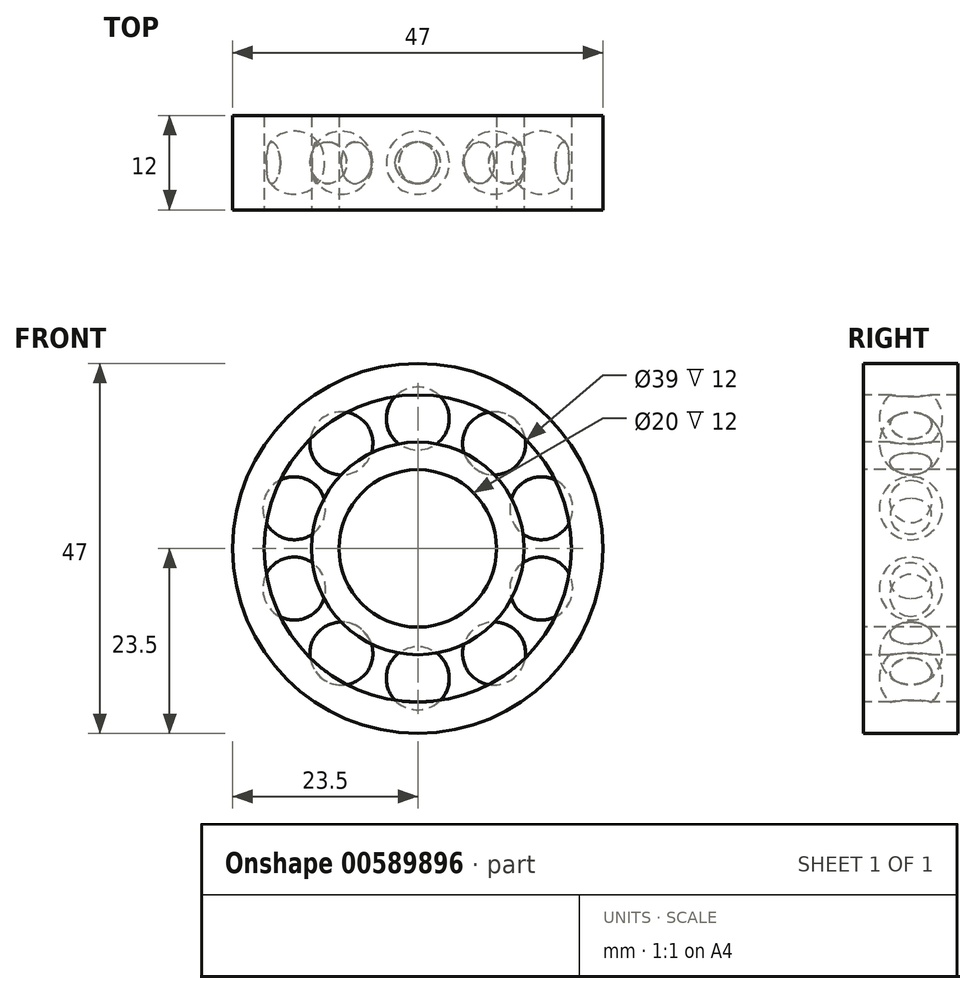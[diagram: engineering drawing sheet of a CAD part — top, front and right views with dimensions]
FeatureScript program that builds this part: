
annotation { "Feature Type Name" : "Feature", "Feature Type Description" : "" }
export const myFeature = defineFeature(function(context is Context, id is Id, definition is map)
    precondition{}
    {
        {
            var Q0;
            Q0=qCreatedBy(makeId("Right.planeOp"),FACE);
            var sketch = newSketch(context, id + "F0", { "sketchPlane" : qUnion([Q0])});
            skLineSegment(sketch, "E0.bottom", {"start": v(0, 23.5) * mm, "end": v(-12, 23.5) * mm});
            skLineSegment(sketch, "E0.top", {"start": v(0, 19.5) * mm, "end": v(-12, 19.5) * mm});
            skLineSegment(sketch, "E0.left", {"start": v(0, 23.5) * mm, "end": v(0, 19.5) * mm});
            skLineSegment(sketch, "E0.right", {"start": v(-12, 23.5) * mm, "end": v(-12, 19.5) * mm});
            skLineSegment(sketch, "E1.bottom", {"start": v(0, 13.5) * mm, "end": v(-12, 13.5) * mm});
            skLineSegment(sketch, "E1.top", {"start": v(0, 10) * mm, "end": v(-12, 10) * mm});
            skLineSegment(sketch, "E1.left", {"start": v(0, 13.5) * mm, "end": v(0, 10) * mm});
            skLineSegment(sketch, "E1.right", {"start": v(-12, 13.5) * mm, "end": v(-12, 10) * mm});
            skLineSegment(sketch, "E2", {"start": v(-37.9, 0) * mm, "end": v(34.15, 0) * mm, "construction": true});
            skSolve(sketch);
        }
        {
            var Q0;
            Q0 = qSketchRegion(id + "F0", true);
            var Q1;
            Q1=sQuery(id+"F0.wireOp",EDGE,"E2");
            revolve(context, id + "F1", {"entities" : qUnion([Q0]), "axis" : qUnion([Q1]), "revolveType" : RevolveType.FULL});
        }
        {
            var Q0;
            Q0=qCreatedBy(makeId("Front.planeOp"),FACE);
            cPlane(context, id + "F2", {"entities" : qUnion([Q0]), "cplaneType" : CPlaneType.OFFSET, "offset" : 6 * mm, "width" : 150 * mm, "height" : 150 * mm});
        }
        {
            var Q0;
            Q0=qCreatedBy(id+"F2.planeOp",FACE);
            var sketch = newSketch(context, id + "F3", { "sketchPlane" : qUnion([Q0])});
            skArc(sketch, "E3", {"start": v(0, 12.5) * mm, "mid": v(4, 16.5) * mm, "end": v(0, 20.5) * mm});
            skLineSegment(sketch, "E4", {"start": v(-32.96, 0) * mm, "end": v(37.33, 0) * mm, "construction": true});
            skLineSegment(sketch, "E5", {"start": v(0, 12.5) * mm, "end": v(0, 20.5) * mm});
            skPoint(sketch, "E6.orphan", {"position": v(0, 6.6) * mm});
            skSolve(sketch);
        }
        {
            var Q0;
            Q0=makeQuery(id+"F3.imprint","IMPRINT",FACE,{"disambiguationData":[TD([[makeQuery(id+"F3.imprint","IMPRINT",EDGE,{"derivedFrom":sQuery(id+"F3.wireOp",EDGE,"E3")}),1.0]])]});
            var Q1;
            Q1=sQuery(id+"F3.wireOp",EDGE,"E3");
            var Q2;
            Q2=sQuery(id+"F3.wireOp",EDGE,"E5");
            revolve(context, id + "F4", {"entities" : qUnion([Q0]), "surfaceEntities" : qUnion([Q1]), "axis" : qUnion([Q2]), "revolveType" : RevolveType.FULL});
        }
        {
            var Q0;
            Q0=qCreatedBy(makeId("Right.planeOp"),FACE);
            var sketch = newSketch(context, id + "F5", { "sketchPlane" : qUnion([Q0])});
            skLineSegment(sketch, "E7", {"start": v(-20.98, 0) * mm, "end": v(6.4, 0) * mm, "construction": true});
            skSolve(sketch);
        }
        {
            var Q0;
            Q0=makeQuery(id+"F4.opRevolve","SWEPT_BODY",BODY,{"disambiguationData":[OSD([sQuery(id+"F3.wireOp",EDGE,"E3")])]});
            var Q1;
            Q1=sQuery(id+"F5.wireOp",EDGE,"E7");
            circularPattern(context, id + "F6", {"operationType" : NewBodyOperationType.ADD, "entities" : qUnion([Q0]), "axis" : qUnion([Q1]), "angle" : 360 * degree, "instanceCount" : 10, "equalSpace" : true});
        }
    });
